# Revit family: Cistern-WCPanGlassCistern-Vitra-VitrusSeries_770-5761-01
name_source: partatom
category: Plumbing Fixtures
revit_build: Autodesk Revit 2017 (Build: 20160225_1515(x64)
units: mm (PartAtom-declared; Revit-internal decimal feet)

## family parameters
Cut with Voids When Loaded = No
Host = Face
OmniClass Number = 23.45.05.21.11
OmniClass Title = Water Closets
Part Type = Normal
Room Calculation Point = No
Round Connector Dimension = Use Diameter
Shared = Yes

## types (4) — shared parameters
BIMobject category = Toilet Cisterns
Brand = Vitra
CW Connection = Yes
Default Elevation = 1000 mm  [stored 3.28084 ft]
Design country = Turkey
First Material = Chrome
HW Connection = No
IFC Classification = Sanitary Terminal
Main Material = Plastic
Manufacturer = Vitra
Manufacturer name = Vitra
MountingType = Assembly to floor
NBS Referans Code = 35-93-90
NBS Referans Description = Wc Cisterns
Nominal Depth (mm) = 120 mm  [stored 0.393701 ft]
Nominal Height (mm) = 1140 mm  [stored 3.74016 ft]
Nominal Width (mm) = 518 mm  [stored 1.69948 ft]
OmniClass Code = 23-31 19 19
OmniClass Description = Water Closets
Product certification = https://vitraglobal.com
Product family = Vitrus Glass Cistern
Secondary Material = Yellow
Technical description = https://www.vitra.com.tr
URL = https://www.vitra.com.tr
Uniclass 2.0 Code = PR-35-93-90
Uniclass 2.0 Description = Wc Cisterns
Uniclass 2015 Code = Pr_40_20_93_89
Uniclass 2015 Name = WC cisterns
Vent Connection = No
Warranty Period (Year) = 10 Years
Waste Connection = Yes
Weight Net (kg) = 30,100
Youtube = https://www.youtube.com
zero-valued in all types: Cost

## per-type parameters (varying)
| type | Article No. (default) | Color | Description | Model | Product Manual | Product SKU | Product data url | Product group | Product url | Third Material |
| Cistern-WCPanGlassCistern-3/6L-Vitra-VitrusSeries_770-5761-01 | 770-5761-01 | Black | Glass Cistern 3/6 Litres Wall-Hung | 770-5761-01 | Glass Cistern 3/6 Litres Wall-Hung | 770-5761-01 |  | Glass Cistern 3/6 Litres | https://www.vitra.com.tr | Glass-Black |
| Cistern-WCPanGlassCistern-3/6L-Vitra-VitrusSeries_770-5760-01 | 770-5760-01 | White | Glass Cistern 3/6 Litres Wall-Hung | 770-5760-01 | Glass Cistern 3/6 Litres Wall-Hung | 770-5760-01 | https://www.vitra.com.tr | Glass Cistern 3/6 Litres |  | Glass-White |
| Cistern-WCPanGlassCistern-2,5/4L-Vitra-VitrusSeries_770-5761-02 | 770-5761-02 | Black | Glass Cistern 2,5/4 Litres Wall-Hung | 770-5761-02 | Glass Cistern 2,5/4 Litres Wall-Hung | 770-5761-02 | https://www.vitra.com.tr | Glass Cistern 2,5/4 Litres |  | Glass-Black |
| Cistern-WCPanGlassCistern-2,5/4L-Vitra-VitrusSeries_770-5760-02 | 770-5760-02 | White | Glass Cistern 2,5/4 Litres Wall-Hung | 770-5760-02 | Glass Cistern 2,5/4 Litres Wall-Hung | 770-5760-02 | https://www.vitra.com.tr | Glass Cistern 3/6 Litres |  | Glass-White |

note: [stored X ft] marks values corroborated as IEEE doubles in the binary element streams (Revit-internal decimal feet)

## geometry (parser evidence)
native form markers: Blend x2, Sweep x3
no freeform markers — native parametric forms only
